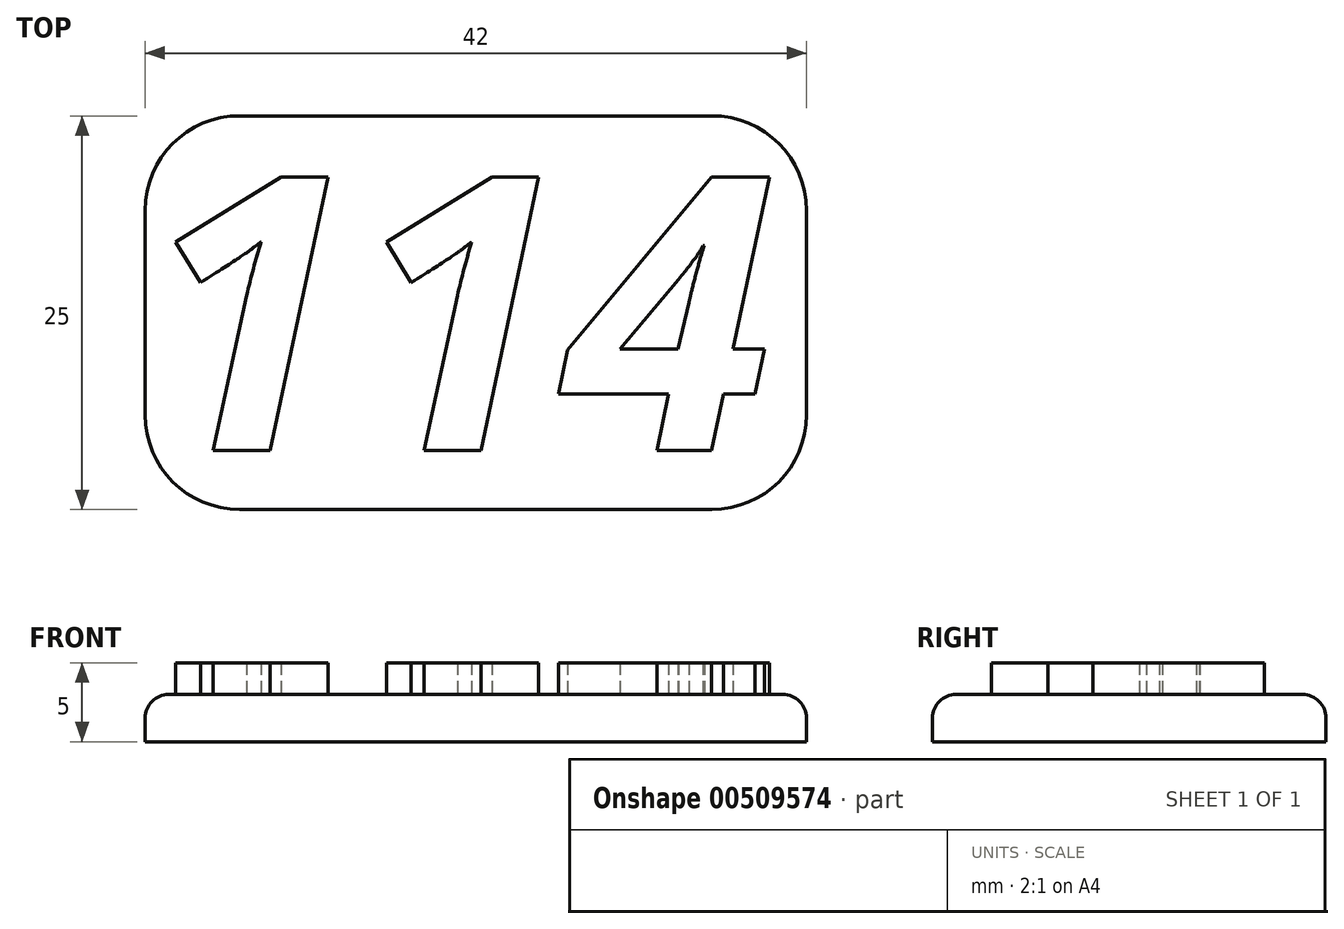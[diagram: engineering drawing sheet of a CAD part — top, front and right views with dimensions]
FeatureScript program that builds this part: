
annotation { "Feature Type Name" : "Feature", "Feature Type Description" : "" }
export const myFeature = defineFeature(function(context is Context, id is Id, definition is map)
    precondition{}
    {
        {
            var Q0;
            Q0=qCreatedBy(makeId("Top.planeOp"),FACE);
            var sketch = newSketch(context, id + "F0", { "sketchPlane" : qUnion([Q0])});
            skLineSegment(sketch, "E0.bottom", {"start": v(21, 12.5) * mm, "end": v(-21, 12.5) * mm});
            skLineSegment(sketch, "E0.top", {"start": v(21, -12.5) * mm, "end": v(-21, -12.5) * mm});
            skLineSegment(sketch, "E0.left", {"start": v(21, 12.5) * mm, "end": v(21, -12.5) * mm});
            skLineSegment(sketch, "E0.right", {"start": v(-21, 12.5) * mm, "end": v(-21, -12.5) * mm});
            skPoint(sketch, "E0.middle", {"position": v(0, 0) * mm});
            skSolve(sketch);
        }
        {
            var Q0;
            Q0=makeQuery(id+"F0.imprint","IMPRINT",FACE,{"disambiguationData":[TD([[makeQuery(id+"F0.imprint","IMPRINT",EDGE,{"derivedFrom":sQuery(id+"F0.wireOp",EDGE,"E0.bottom")}),1.0]])]});
            extrude(context, id + "F1", {"entities" : qUnion([Q0]), "depth" : 3 * mm});
        }
        {
            var Q0;
            Q0=makeQuery(id+"F1.opExtrude","SWEPT_EDGE",EDGE,{"disambiguationData":[OSD([sQuery(id+"F0.wireOp",EDGE,"E0.top"),sQuery(id+"F0.wireOp",EDGE,"E0.right")])]});
            var Q1;
            Q1=makeQuery(id+"F1.opExtrude","SWEPT_EDGE",EDGE,{"disambiguationData":[OSD([sQuery(id+"F0.wireOp",EDGE,"E0.top"),sQuery(id+"F0.wireOp",EDGE,"E0.left")])]});
            var Q2;
            Q2=makeQuery(id+"F1.opExtrude","SWEPT_EDGE",EDGE,{"disambiguationData":[OSD([sQuery(id+"F0.wireOp",EDGE,"E0.bottom"),sQuery(id+"F0.wireOp",EDGE,"E0.right")])]});
            var Q3;
            Q3=makeQuery(id+"F1.opExtrude","SWEPT_EDGE",EDGE,{"disambiguationData":[OSD([sQuery(id+"F0.wireOp",EDGE,"E0.bottom"),sQuery(id+"F0.wireOp",EDGE,"E0.left")])]});
            fillet(context, id + "F2", {"entities" : qUnion([Q0, Q1, Q2, Q3]), "radius" : 6 * mm, "tangentPropagation" : true, "allowEdgeOverflow" : false});
        }
        {
            var Q0;
            Q0=makeQuery(id+"F1.opExtrude","CAP_EDGE",EDGE,{"disambiguationData":[OSD([sQuery(id+"F0.wireOp",EDGE,"E0.top")])],"isStart":false});
            fillet(context, id + "F3", {"entities" : qUnion([Q0]), "radius" : 1.5 * mm, "tangentPropagation" : true, "allowEdgeOverflow" : false});
        }
        {
            var Q0;
            Q0=makeQuery(id+"F1.opExtrude","CAP_FACE",FACE,{"disambiguationData":[OSD([sQuery(id+"F0.wireOp",EDGE,"E0.bottom"),sQuery(id+"F0.wireOp",EDGE,"E0.top"),sQuery(id+"F0.wireOp",EDGE,"E0.left"),sQuery(id+"F0.wireOp",EDGE,"E0.right")])],"isStart":false});
            var sketch = newSketch(context, id + "F4", { "sketchPlane" : qUnion([Q0])});
            skText(sketch, "E1", { "text": "114", "fontName": "OpenSans-BoldItalic.ttf"});
            const initialGuessF4  = {"E1": [-0.02123, -0.00875, 1, 0, 0.0175]};
            skSetInitialGuess(sketch, initialGuessF4);
            skSolve(sketch);
        }
        {
            var Q0;
            Q0 = qSketchRegion(id + "F4", true);
            extrude(context, id + "F5", {"entities" : qUnion([Q0]), "operationType" : NewBodyOperationType.ADD, "depth" : 2 * mm});
        }
    });
